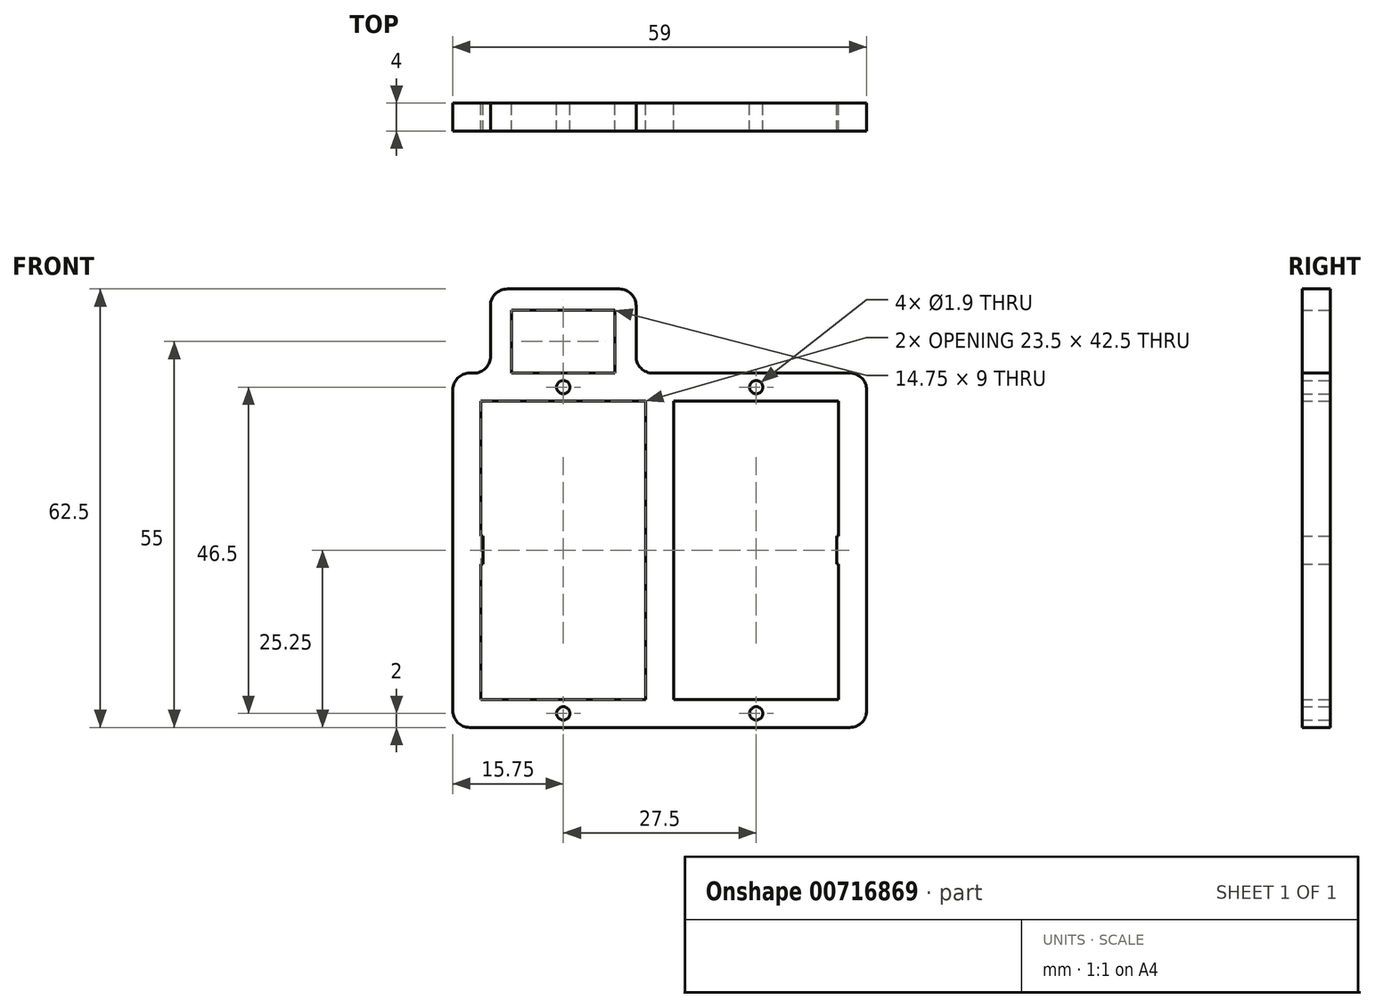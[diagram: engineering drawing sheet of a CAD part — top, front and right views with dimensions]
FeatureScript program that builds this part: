
annotation { "Feature Type Name" : "Feature", "Feature Type Description" : "" }
export const myFeature = defineFeature(function(context is Context, id is Id, definition is map)
    precondition{}
    {
        {
            var Q0;
            Q0=qCreatedBy(makeId("Front.planeOp"),FACE);
            var sketch = newSketch(context, id + "F0", { "sketchPlane" : qUnion([Q0])});
            skLineSegment(sketch, "E0", {"start": v(2, 0) * mm, "end": v(2, 42.5) * mm});
            skLineSegment(sketch, "E1", {"start": v(2, 42.5) * mm, "end": v(25.5, 42.5) * mm});
            skLineSegment(sketch, "E2", {"start": v(25.5, 42.5) * mm, "end": v(25.5, 23.25) * mm});
            skLineSegment(sketch, "E3", {"start": v(25.5, 0) * mm, "end": v(2, 0) * mm});
            skLineSegment(sketch, "E4.MirrorCS", {"start": v(-2, 0) * mm, "end": v(-2, 42.5) * mm});
            skLineSegment(sketch, "E5.MirrorCS", {"start": v(-2, 42.5) * mm, "end": v(-25.5, 42.5) * mm});
            skLineSegment(sketch, "E6.MirrorCS", {"start": v(-25.5, 42.5) * mm, "end": v(-25.5, 23.25) * mm});
            skLineSegment(sketch, "E7.MirrorCS", {"start": v(-25.5, 0) * mm, "end": v(-2, 0) * mm});
            skLineSegment(sketch, "E8", {"start": v(-29.5, 46.5) * mm, "end": v(-24.12, 46.5) * mm});
            skLineSegment(sketch, "E9", {"start": v(29.5, 46.5) * mm, "end": v(29.5, -4) * mm});
            skLineSegment(sketch, "E10", {"start": v(29.5, -4) * mm, "end": v(-29.5, -4) * mm});
            skLineSegment(sketch, "E11", {"start": v(-29.5, -4) * mm, "end": v(-29.5, 46.5) * mm});
            skPoint(sketch, "E12", {"position": v(-13.75, 46.5) * mm});
            skPoint(sketch, "E12.positionSnap0", {"position": v(-13.75, 42.5) * mm});
            skLineSegment(sketch, "E13", {"start": v(-21.12, 46.5) * mm, "end": v(-21.12, 55.5) * mm});
            skLineSegment(sketch, "E14", {"start": v(-21.12, 55.5) * mm, "end": v(-6.37, 55.5) * mm});
            skLineSegment(sketch, "E15", {"start": v(-6.37, 55.5) * mm, "end": v(-6.37, 46.5) * mm});
            skPoint(sketch, "E16", {"position": v(-13.75, 55.5) * mm});
            skLineSegment(sketch, "E17", {"start": v(-24.12, 46.5) * mm, "end": v(-24.12, 58.5) * mm});
            skLineSegment(sketch, "E18", {"start": v(-24.12, 58.5) * mm, "end": v(-3.37, 58.5) * mm});
            skLineSegment(sketch, "E19", {"start": v(-3.37, 58.5) * mm, "end": v(-3.37, 46.5) * mm});
            skLineSegment(sketch, "E20.trimOffspring", {"start": v(-3.37, 46.5) * mm, "end": v(29.5, 46.5) * mm});
            skLineSegment(sketch, "E21.trimOffspring", {"start": v(-21.12, 46.5) * mm, "end": v(-6.37, 46.5) * mm});
            skPoint(sketch, "E22", {"position": v(-25.5, 21.25) * mm});
            skLineSegment(sketch, "E23", {"start": v(-25.5, 23.25) * mm, "end": v(-25.2, 23.25) * mm});
            skLineSegment(sketch, "E24", {"start": v(-25.2, 23.25) * mm, "end": v(-25.2, 19.25) * mm});
            skLineSegment(sketch, "E25", {"start": v(-25.2, 19.25) * mm, "end": v(-25.5, 19.25) * mm});
            skPoint(sketch, "E26", {"position": v(-25.2, 21.25) * mm});
            skLineSegment(sketch, "E27.MirrorCS", {"start": v(25.2, 23.25) * mm, "end": v(25.2, 19.25) * mm});
            skLineSegment(sketch, "E28.MirrorCS", {"start": v(25.5, 23.25) * mm, "end": v(25.2, 23.25) * mm});
            skLineSegment(sketch, "E29.MirrorCS", {"start": v(25.2, 19.25) * mm, "end": v(25.5, 19.25) * mm});
            skLineSegment(sketch, "E30.trimOffspring", {"start": v(25.5, 19.25) * mm, "end": v(25.5, 0) * mm});
            skLineSegment(sketch, "E31.trimOffspring", {"start": v(-25.5, 19.25) * mm, "end": v(-25.5, 0) * mm});
            skLineSegment(sketch, "E32", {"start": v(-9.84, 42.5) * mm, "end": v(-9.84, 46.5) * mm, "construction": true});
            skPoint(sketch, "E33", {"position": v(-13.75, 44.5) * mm});
            skPoint(sketch, "E33.positionSnap0", {"position": v(-9.84, 44.5) * mm});
            skPoint(sketch, "E34", {"position": v(13.75, 44.5) * mm});
            skPoint(sketch, "E34.positionSnap0", {"position": v(13.75, 42.5) * mm});
            skLineSegment(sketch, "E35", {"start": v(-2.67, 0) * mm, "end": v(-2.67, -4) * mm, "construction": true});
            skPoint(sketch, "E36", {"position": v(-13.75, -2) * mm});
            skPoint(sketch, "E36.positionSnap0", {"position": v(-13.75, 0) * mm});
            skPoint(sketch, "E36.positionSnap1", {"position": v(-2.67, -2) * mm});
            skPoint(sketch, "E37", {"position": v(13.75, -2) * mm});
            skPoint(sketch, "E37.positionSnap0", {"position": v(13.75, 0) * mm});
            skSolve(sketch);
        }
        {
            var Q0;
            Q0=makeQuery(id+"F0.imprint","IMPRINT",FACE,{"disambiguationData":[TD([[makeQuery(id+"F0.imprint","IMPRINT",EDGE,{"derivedFrom":sQuery(id+"F0.wireOp",EDGE,"E0")}),1.0]])]});
            extrude(context, id + "F1", {"entities" : qUnion([Q0]), "depth" : 4 * mm, "offsetDistance" : 25 * mm});
        }
        {
            var Q0;
            Q0=makeQuery(id+"F1.opExtrude","SWEPT_EDGE",EDGE,{"disambiguationData":[OSD([sQuery(id+"F0.wireOp",EDGE,"E17"),sQuery(id+"F0.wireOp",EDGE,"E18")])]});
            var Q1;
            Q1=makeQuery(id+"F1.opExtrude","SWEPT_EDGE",EDGE,{"disambiguationData":[OSD([sQuery(id+"F0.wireOp",EDGE,"E8"),sQuery(id+"F0.wireOp",EDGE,"E17")])]});
            var Q2;
            Q2=makeQuery(id+"F1.opExtrude","SWEPT_EDGE",EDGE,{"disambiguationData":[OSD([sQuery(id+"F0.wireOp",EDGE,"E8"),sQuery(id+"F0.wireOp",EDGE,"E11")])]});
            var Q3;
            Q3=makeQuery(id+"F1.opExtrude","SWEPT_EDGE",EDGE,{"disambiguationData":[OSD([sQuery(id+"F0.wireOp",EDGE,"E18"),sQuery(id+"F0.wireOp",EDGE,"E19")])]});
            var Q4;
            Q4=makeQuery(id+"F1.opExtrude","SWEPT_EDGE",EDGE,{"disambiguationData":[OSD([sQuery(id+"F0.wireOp",EDGE,"E9"),sQuery(id+"F0.wireOp",EDGE,"E20.trimOffspring")])]});
            var Q5;
            Q5=makeQuery(id+"F1.opExtrude","SWEPT_EDGE",EDGE,{"disambiguationData":[OSD([sQuery(id+"F0.wireOp",EDGE,"E19"),sQuery(id+"F0.wireOp",EDGE,"E20.trimOffspring")])]});
            var Q6;
            Q6=makeQuery(id+"F1.opExtrude","SWEPT_EDGE",EDGE,{"disambiguationData":[OSD([sQuery(id+"F0.wireOp",EDGE,"E9"),sQuery(id+"F0.wireOp",EDGE,"E10")])]});
            var Q7;
            Q7=makeQuery(id+"F1.opExtrude","SWEPT_EDGE",EDGE,{"disambiguationData":[OSD([sQuery(id+"F0.wireOp",EDGE,"E10"),sQuery(id+"F0.wireOp",EDGE,"E11")])]});
            fillet(context, id + "F2", {"entities" : qUnion([Q0, Q1, Q2, Q3, Q4, Q5, Q6, Q7]), "radius" : 2.4 * mm, "tangentPropagation" : true, "allowEdgeOverflow" : false});
        }
        {
            var Q0;
            Q0=sQuery(id+"F0.wireOp",VERTEX,"E36");
            var Q1;
            Q1=sQuery(id+"F0.wireOp",VERTEX,"E37");
            var Q2;
            Q2=sQuery(id+"F0.wireOp",VERTEX,"E33");
            var Q3;
            Q3=sQuery(id+"F0.wireOp",VERTEX,"E34");
            var Q4;
            Q4=makeQuery(id+"F1.opExtrude","SWEPT_BODY",BODY,{"disambiguationData":[OSD([sQuery(id+"F0.wireOp",EDGE,"E0"),sQuery(id+"F0.wireOp",EDGE,"E1"),sQuery(id+"F0.wireOp",EDGE,"E2"),sQuery(id+"F0.wireOp",EDGE,"E3"),sQuery(id+"F0.wireOp",EDGE,"E4.MirrorCS"),sQuery(id+"F0.wireOp",EDGE,"E5.MirrorCS"),sQuery(id+"F0.wireOp",EDGE,"E6.MirrorCS"),sQuery(id+"F0.wireOp",EDGE,"E7.MirrorCS"),sQuery(id+"F0.wireOp",EDGE,"E8"),sQuery(id+"F0.wireOp",EDGE,"E9"),sQuery(id+"F0.wireOp",EDGE,"E10"),sQuery(id+"F0.wireOp",EDGE,"E11"),sQuery(id+"F0.wireOp",EDGE,"E13"),sQuery(id+"F0.wireOp",EDGE,"E14"),sQuery(id+"F0.wireOp",EDGE,"E15"),sQuery(id+"F0.wireOp",EDGE,"E17"),sQuery(id+"F0.wireOp",EDGE,"E18"),sQuery(id+"F0.wireOp",EDGE,"E19"),sQuery(id+"F0.wireOp",EDGE,"E20.trimOffspring"),sQuery(id+"F0.wireOp",EDGE,"E21.trimOffspring"),sQuery(id+"F0.wireOp",EDGE,"E23"),sQuery(id+"F0.wireOp",EDGE,"E24"),sQuery(id+"F0.wireOp",EDGE,"E25"),sQuery(id+"F0.wireOp",EDGE,"E27.MirrorCS"),sQuery(id+"F0.wireOp",EDGE,"E28.MirrorCS"),sQuery(id+"F0.wireOp",EDGE,"E29.MirrorCS"),sQuery(id+"F0.wireOp",EDGE,"E30.trimOffspring"),sQuery(id+"F0.wireOp",EDGE,"E31.trimOffspring")])]});
            hole(context, id + "F3", {"style" : HoleStyle.SIMPLE, "endStyle" : HoleEndStyle.THROUGH, "oppositeDirection" : true, "holeDiameter" : 1.9 * mm, "majorDiameter" : 5 * mm, "tappedDepth" : 12 * mm, "tapClearance" : 3, "locations" : qUnion([Q0, Q1, Q2, Q3]), "scope" : qUnion([Q4])});
        }
    });
